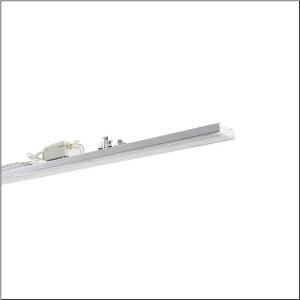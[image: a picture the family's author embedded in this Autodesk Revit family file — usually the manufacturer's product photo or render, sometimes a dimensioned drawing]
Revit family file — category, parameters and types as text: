
# Revit family: licross_r__21_recessed_mo_52tl11dn4axg_0374
name_source: partatom
category: Lighting Fixtures
units: mm (PartAtom-declared; Revit-internal decimal feet)

## family parameters
Cut with Voids When Loaded = No
Host = Face
Light Source = No
Part Type = Normal
Room Calculation Point = No
Round Connector Dimension = Use Diameter
Shared = No

## types (1)
- --- (1 x LED, 10120 lm, 58 W, 4000K)
    Apparent Load = 58 VA
    CIE Flux Codes = 89 96 99 100 100
    Color Rendering = 80
    Color Temperature = 4000K
    Default Elevation = 1800 mm
    Description = Licross® 21 Recessed MO, luminaire insert, of sheet steel, galvanised, coil coated, white, length: 1.500mm, width: 66mm, height: 67mm, LED rated luminous flux: 10.120lm, light colour: 840, control gear: DALI 2, with plug, 5-pole, with phase selection, mains connection: 220..240V, AC, 50/60Hz, rated input power: 58W, halogen-free wiring, primary light control with lens, of plastic, primary optical cover: cover, of PMMA, light emission: direct distribution, primary light characteristic: symmetric, protection rating (complete): IP40, insulation class (complete): insulation class I (protective earthing), certification: CE, ENEC, VDE, UKCA, protection symbol: D if used in an environment without relevant dust loads with corresponding accessories, impact resistance: IK06, permissible ambient temperature for indoor applications: -25..+40°C, corresponds to IFS (International Featured Standards) requirements for safety and quality in the food industry, reducing of maximum allowable ambient temperature of 5°C with ceiling mounting, LABS conformity tested according to VDMA 24364:2018-05, packaging unit: 1 piece
    Height = 58 mm
    Lamp = 1 x LED
    Lamp Light Flux = 10120 lm
    Lamp Power = 58 W
    Lamp count = 1
    Length = 1500 mm
    Luminous efficacy = 174 lm/W
    Manufacturer = Siteco
    ModVariant = No
    Model = 52TL11DN4AXG
    Mounting Place = Ceiling
    Mounting Type = Pendant
    Number of Poles = 1
    OnlyDefault = Yes
    Power Factor = 1
    Product Name = Licross® 21 Recessed MO
    Product group = luminaire insert
    ProductGroupID = 901
    Protection Class = Protection class I
    Protection Degree = IP 40
    RLX_Detail_Level = 1
    RLX_Emergency_Light_Flux = 0 lm
    RLX_Emergency_Type = 0
    RLX_Emergency_Type_DB = No
    RlxData = <blob elided: 24513 chars, md5=b1a07f96>
    Socket = socket
    Standby Power = 0 W
    System Light Flux = 10120 lm
    System Power = 58 W
    Type Comments = factory setting: luminous flux: 100 % | dim-lin: 254 | 390 mA
    Type Image = l_1296930.jpg
    URL = http://relux.com
    VarID = @adj_058577
    Voltage = 0 V
    Weight = 0.00 kg
    Width = 66 mm

## geometry (parser evidence)
native form markers: Blend x4, Sweep x13
no freeform markers — native parametric forms only
